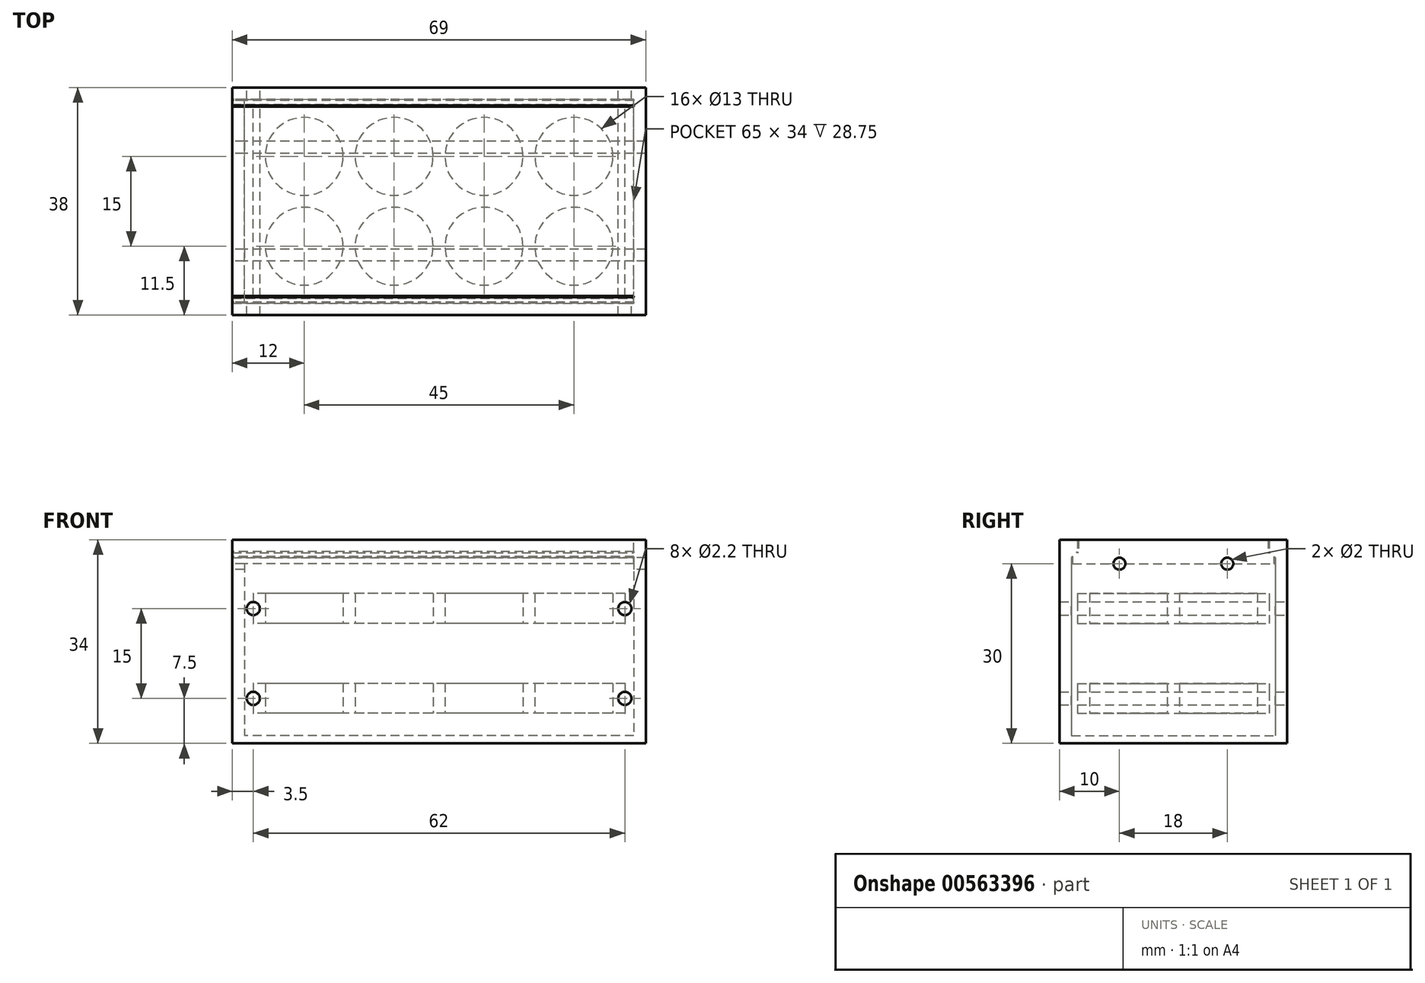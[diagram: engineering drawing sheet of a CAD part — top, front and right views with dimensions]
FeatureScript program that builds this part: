
annotation { "Feature Type Name" : "Feature", "Feature Type Description" : "" }
export const myFeature = defineFeature(function(context is Context, id is Id, definition is map)
    precondition{}
    {
        {
            var Q0;
            Q0=qCreatedBy(makeId("Top.planeOp"),FACE);
            var sketch = newSketch(context, id + "F0", { "sketchPlane" : qUnion([Q0])});
            skCircle(sketch, "E0", {"center": v(0, 0) * mm, "radius": 6.5 * mm});
            skCircle(sketch, "E1.0.1.0", {"center": v(0, 15) * mm, "radius": 6.5 * mm});
            skCircle(sketch, "E1.1.0.0", {"center": v(15, 0) * mm, "radius": 6.5 * mm});
            skCircle(sketch, "E1.1.1.0", {"center": v(15, 15) * mm, "radius": 6.5 * mm});
            skCircle(sketch, "E1.2.0.0", {"center": v(30, 0) * mm, "radius": 6.5 * mm});
            skCircle(sketch, "E1.2.1.0", {"center": v(30, 15) * mm, "radius": 6.5 * mm});
            skCircle(sketch, "E1.3.0.0", {"center": v(45, 0) * mm, "radius": 6.5 * mm});
            skCircle(sketch, "E1.3.1.0", {"center": v(45, 15) * mm, "radius": 6.5 * mm});
            skLineSegment(sketch, "E1.direction1", {"start": v(0, 0) * mm, "end": v(15, 0) * mm, "construction": true});
            skLineSegment(sketch, "E1.direction2", {"start": v(0, 0) * mm, "end": v(0, 15) * mm, "construction": true});
            skLineSegment(sketch, "E2.bottom", {"start": v(53.5, -8.5) * mm, "end": v(-8.5, -8.5) * mm});
            skLineSegment(sketch, "E2.top", {"start": v(53.5, 23.5) * mm, "end": v(-8.5, 23.5) * mm});
            skLineSegment(sketch, "E2.left", {"start": v(53.5, -8.5) * mm, "end": v(53.5, 23.5) * mm});
            skLineSegment(sketch, "E2.right", {"start": v(-8.5, -8.5) * mm, "end": v(-8.5, 23.5) * mm});
            skPoint(sketch, "E2.middle", {"position": v(22.5, 7.5) * mm});
            skPoint(sketch, "E2.middle.positionSnap0", {"position": v(0, 7.5) * mm});
            skPoint(sketch, "E2.centerSnap0", {"position": v(0, 7.5) * mm});
            skLineSegment(sketch, "E3", {"start": v(45, 15) * mm, "end": v(45, 0) * mm, "construction": true});
            skLineSegment(sketch, "E4", {"start": v(45, 7.5) * mm, "end": v(0, 7.5) * mm, "construction": true});
            skLineSegment(sketch, "E5.bottom", {"start": v(57, -11.5) * mm, "end": v(-12, -11.5) * mm});
            skLineSegment(sketch, "E5.top", {"start": v(57, 26.5) * mm, "end": v(-12, 26.5) * mm});
            skLineSegment(sketch, "E5.left", {"start": v(57, -11.5) * mm, "end": v(57, 26.5) * mm});
            skLineSegment(sketch, "E5.right", {"start": v(-12, -11.5) * mm, "end": v(-12, 26.5) * mm});
            skLineSegment(sketch, "E6.bottom", {"start": v(55, -9.5) * mm, "end": v(-10, -9.5) * mm});
            skLineSegment(sketch, "E6.top", {"start": v(55, 24.5) * mm, "end": v(-10, 24.5) * mm});
            skLineSegment(sketch, "E6.left", {"start": v(55, -9.5) * mm, "end": v(55, 24.5) * mm});
            skLineSegment(sketch, "E6.right", {"start": v(-10, -9.5) * mm, "end": v(-10, 24.5) * mm});
            skSolve(sketch);
        }
        {
            var Q0;
            Q0=makeQuery(id+"F0.imprint","IMPRINT",FACE,{"disambiguationData":[TD([[makeQuery(id+"F0.imprint","IMPRINT",EDGE,{"derivedFrom":sQuery(id+"F0.wireOp",EDGE,"E5.bottom")}),-1.0]])]});
            extrude(context, id + "F1", {"entities" : qUnion([Q0]), "depth" : 30 * mm, "offsetDistance" : 25 * mm});
        }
        {
            var Q0;
            Q0=makeQuery(id+"F0.imprint","IMPRINT",FACE,{"disambiguationData":[TD([[makeQuery(id+"F0.imprint","IMPRINT",EDGE,{"derivedFrom":sQuery(id+"F0.wireOp",EDGE,"E2.bottom")}),1.0]])]});
            var Q1;
            Q1=makeQuery(id+"F0.imprint","IMPRINT",FACE,{"disambiguationData":[TD([[makeQuery(id+"F0.imprint","IMPRINT",EDGE,{"derivedFrom":sQuery(id+"F0.wireOp",EDGE,"E1.0.1.0")}),1.0]])]});
            var Q2;
            Q2=makeQuery(id+"F0.imprint","IMPRINT",FACE,{"disambiguationData":[TD([[makeQuery(id+"F0.imprint","IMPRINT",EDGE,{"derivedFrom":sQuery(id+"F0.wireOp",EDGE,"E1.1.1.0")}),1.0]])]});
            var Q3;
            Q3=makeQuery(id+"F0.imprint","IMPRINT",FACE,{"disambiguationData":[TD([[makeQuery(id+"F0.imprint","IMPRINT",EDGE,{"derivedFrom":sQuery(id+"F0.wireOp",EDGE,"E1.2.1.0")}),1.0]])]});
            var Q4;
            Q4=makeQuery(id+"F0.imprint","IMPRINT",FACE,{"disambiguationData":[TD([[makeQuery(id+"F0.imprint","IMPRINT",EDGE,{"derivedFrom":sQuery(id+"F0.wireOp",EDGE,"E1.3.1.0")}),1.0]])]});
            var Q5;
            Q5=makeQuery(id+"F0.imprint","IMPRINT",FACE,{"disambiguationData":[TD([[makeQuery(id+"F0.imprint","IMPRINT",EDGE,{"derivedFrom":sQuery(id+"F0.wireOp",EDGE,"E1.3.0.0")}),1.0]])]});
            var Q6;
            Q6=makeQuery(id+"F0.imprint","IMPRINT",FACE,{"disambiguationData":[TD([[makeQuery(id+"F0.imprint","IMPRINT",EDGE,{"derivedFrom":sQuery(id+"F0.wireOp",EDGE,"E1.1.0.0")}),1.0]])]});
            var Q7;
            Q7=makeQuery(id+"F0.imprint","IMPRINT",FACE,{"disambiguationData":[TD([[makeQuery(id+"F0.imprint","IMPRINT",EDGE,{"derivedFrom":sQuery(id+"F0.wireOp",EDGE,"E0")}),-1.0]])]});
            var Q8;
            Q8=makeQuery(id+"F0.imprint","IMPRINT",FACE,{"disambiguationData":[TD([[makeQuery(id+"F0.imprint","IMPRINT",EDGE,{"derivedFrom":sQuery(id+"F0.wireOp",EDGE,"E1.2.0.0")}),1.0]])]});
            var Q9;
            Q9=makeQuery(id+"F0.imprint","IMPRINT",FACE,{"disambiguationData":[TD([[makeQuery(id+"F0.imprint","IMPRINT",EDGE,{"derivedFrom":sQuery(id+"F0.wireOp",EDGE,"E0")}),1.0]])]});
            extrude(context, id + "F2", {"entities" : qUnion([Q0, Q1, Q2, Q3, Q4, Q5, Q6, Q7, Q8, Q9]), "operationType" : NewBodyOperationType.ADD, "depth" : 1.25 * mm, "offsetDistance" : 25 * mm});
        }
        {
            var Q0;
            Q0=makeQuery(id+"F0.imprint","IMPRINT",FACE,{"disambiguationData":[TD([[makeQuery(id+"F0.imprint","IMPRINT",EDGE,{"derivedFrom":sQuery(id+"F0.wireOp",EDGE,"E0")}),-1.0]])]});
            extrude(context, id + "F3", {"entities" : qUnion([Q0]), "depth" : 10 * mm, "offsetDistance" : 25 * mm, "hasSecondDirection" : true, "secondDirectionOppositeDirection" : false, "secondDirectionDepth" : 5 * mm});
        }
        {
            var Q0;
            Q0=makeQuery(id+"F3.opExtrude","SWEPT_BODY",BODY,{"disambiguationData":[OSD([sQuery(id+"F0.wireOp",EDGE,"E0"),sQuery(id+"F0.wireOp",EDGE,"E1.0.1.0"),sQuery(id+"F0.wireOp",EDGE,"E1.1.0.0"),sQuery(id+"F0.wireOp",EDGE,"E1.1.1.0"),sQuery(id+"F0.wireOp",EDGE,"E1.2.0.0"),sQuery(id+"F0.wireOp",EDGE,"E1.2.1.0"),sQuery(id+"F0.wireOp",EDGE,"E1.3.0.0"),sQuery(id+"F0.wireOp",EDGE,"E1.3.1.0"),sQuery(id+"F0.wireOp",EDGE,"E2.bottom"),sQuery(id+"F0.wireOp",EDGE,"E2.top"),sQuery(id+"F0.wireOp",EDGE,"E2.left"),sQuery(id+"F0.wireOp",EDGE,"E2.right")])]});
            transform(context, id + "F4", {"entities" : qUnion([Q0]), "transformType" : TransformType.TRANSLATION_3D, "dx" : 0 * mm, "dy" : 0 * mm, "dz" : 15 * mm, "makeCopy" : true});
        }
        {
            var Q0;
            Q0=makeQuery(id+"F1.opExtrude","SWEPT_FACE",FACE,{"disambiguationData":[OSD([sQuery(id+"F0.wireOp",EDGE,"E5.top")])]});
            var sketch = newSketch(context, id + "F5", { "sketchPlane" : qUnion([Q0])});
            skCircle(sketch, "E7", {"center": v(8.5, 22.5) * mm, "radius": 1.1 * mm});
            skCircle(sketch, "E8", {"center": v(8.5, 7.5) * mm, "radius": 1.1 * mm});
            skCircle(sketch, "E9", {"center": v(-53.5, 7.5) * mm, "radius": 1.1 * mm});
            skCircle(sketch, "E10", {"center": v(-53.5, 22.5) * mm, "radius": 1.1 * mm});
            skSolve(sketch);
        }
        {
            var Q0;
            Q0 = qSketchRegion(id + "F5", true);
            extrude(context, id + "F6", {"entities" : qUnion([Q0]), "operationType" : NewBodyOperationType.REMOVE, "endBound" : BoundingType.SYMMETRIC, "oppositeDirection" : true, "depth" : 100 * mm, "offsetDistance" : 25 * mm});
        }
        {
            var Q0;
            Q0=makeQuery(id+"F1.opExtrude","SWEPT_FACE",FACE,{"disambiguationData":[OSD([sQuery(id+"F0.wireOp",EDGE,"E5.right")])]});
            var sketch = newSketch(context, id + "F7", { "sketchPlane" : qUnion([Q0])});
            skLineSegment(sketch, "E11", {"start": v(-26.5, 30) * mm, "end": v(-26.5, 34) * mm});
            skLineSegment(sketch, "E12", {"start": v(-26.5, 34) * mm, "end": v(-23.5, 34) * mm});
            skLineSegment(sketch, "E13", {"start": v(-23.5, 34) * mm, "end": v(-23.5, 32) * mm});
            skLineSegment(sketch, "E14", {"start": v(-23.5, 32) * mm, "end": v(-24.5, 32) * mm});
            skLineSegment(sketch, "E15", {"start": v(-24.5, 32) * mm, "end": v(-24.5, 30) * mm});
            skLineSegment(sketch, "E16", {"start": v(-7.5, 30) * mm, "end": v(-7.5, 34.07) * mm, "construction": true});
            skPoint(sketch, "E16.endSnap0", {"position": v(-7.5, 30) * mm});
            skLineSegment(sketch, "E17.MirrorCS", {"start": v(8.5, 32) * mm, "end": v(9.5, 32) * mm});
            skLineSegment(sketch, "E18.MirrorCS", {"start": v(11.5, 34) * mm, "end": v(8.5, 34) * mm});
            skLineSegment(sketch, "E19.MirrorCS", {"start": v(11.5, 30) * mm, "end": v(11.5, 34) * mm});
            skLineSegment(sketch, "E20.MirrorCS", {"start": v(8.5, 34) * mm, "end": v(8.5, 32) * mm});
            skLineSegment(sketch, "E21.MirrorCS", {"start": v(9.5, 32) * mm, "end": v(9.5, 30) * mm});
            skLineSegment(sketch, "E22", {"start": v(8.5, 34) * mm, "end": v(-23.5, 34) * mm});
            skLineSegment(sketch, "E23", {"start": v(-23.3, 34) * mm, "end": v(-23.3, 31.8) * mm});
            skLineSegment(sketch, "E24", {"start": v(-23.3, 31.8) * mm, "end": v(-24.3, 31.8) * mm});
            skLineSegment(sketch, "E25", {"start": v(-24.3, 31.8) * mm, "end": v(-24.3, 30) * mm});
            skLineSegment(sketch, "E26.MirrorCS", {"start": v(8.3, 34) * mm, "end": v(8.3, 31.8) * mm});
            skLineSegment(sketch, "E27.MirrorCS", {"start": v(8.3, 31.8) * mm, "end": v(9.3, 31.8) * mm});
            skLineSegment(sketch, "E28.MirrorCS", {"start": v(9.3, 31.8) * mm, "end": v(9.3, 30) * mm});
            skSolve(sketch);
        }
        {
            var Q0;
            {var subQ0=sQuery(id+"F7.wireOp",EDGE,"E11");Q0=makeQuery(id+"F7.imprint","IMPRINT",FACE,{"disambiguationData":[TD([[makeQuery(id+"F7.imprint","IMPRINT",EDGE,{"derivedFrom":subQ0}),-1.0]])]});}
            var Q1;
            Q1=makeQuery(id+"F7.imprint","IMPRINT",FACE,{"disambiguationData":[TD([[makeQuery(id+"F7.imprint","IMPRINT",EDGE,{"derivedFrom":sQuery(id+"F7.wireOp",EDGE,"E17.MirrorCS")}),1.0]])]});
            var Q2;
            Q2=makeQuery(id+"F1.opExtrude","SWEPT_FACE",FACE,{"disambiguationData":[OSD([sQuery(id+"F0.wireOp",EDGE,"E5.left")])]});
            extrude(context, id + "F8", {"entities" : qUnion([Q0, Q1]), "operationType" : NewBodyOperationType.ADD, "endBound" : BoundingType.UP_TO_SURFACE, "oppositeDirection" : true, "depth" : 25 * mm, "endBoundEntityFace" : qUnion([Q2]), "offsetDistance" : 25 * mm});
        }
        {
            var Q0;
            Q0=makeQuery(id+"F8.opExtrude","SWEPT_EDGE",EDGE,{"disambiguationData":[OSD([sQuery(id+"F7.wireOp",EDGE,"E14"),sQuery(id+"F7.wireOp",EDGE,"E15")])]});
            var Q1;
            Q1=makeQuery(id+"F8.opExtrude","SWEPT_EDGE",EDGE,{"disambiguationData":[OSD([sQuery(id+"F7.wireOp",EDGE,"E17.MirrorCS"),sQuery(id+"F7.wireOp",EDGE,"E21.MirrorCS")])]});
            chamfer(context, id + "F9", {"entities" : qUnion([Q0, Q1]), "width" : 1 * mm, "tangentPropagation" : true});
        }
        {
            var Q0;
            {var subQ3=sQuery(id+"F7.wireOp",EDGE,"E23");Q0=makeQuery(id+"F7.imprint","IMPRINT",FACE,{"disambiguationData":[TD([[makeQuery(id+"F7.imprint","IMPRINT",EDGE,{"derivedFrom":subQ3}),1.0]])]});}
            var Q1;
            Q1=makeQuery(id+"F1.opExtrude","SWEPT_FACE",FACE,{"disambiguationData":[OSD([sQuery(id+"F0.wireOp",EDGE,"E6.left")])]});
            extrude(context, id + "F10", {"entities" : qUnion([Q0]), "endBound" : BoundingType.UP_TO_SURFACE, "oppositeDirection" : true, "depth" : 25 * mm, "endBoundEntityFace" : qUnion([Q1]), "offsetDistance" : 25 * mm});
        }
        {
            var Q0;
            {var subQ0=sQuery(id+"F0.wireOp",EDGE,"E6.left");var subQ1=sQuery(id+"F0.wireOp",EDGE,"E5.left");var subQ2=sQuery(id+"F0.wireOp",EDGE,"E6.top");var subQ3=sQuery(id+"F0.wireOp",EDGE,"E6.bottom");Q0=makeQuery(id+"F8.boolean.opBoolean","SPLIT",FACE,{"disambiguationData":[TD([makeQuery(id+"F1.opExtrude","SWEPT_FACE",FACE,{"disambiguationData":[OSD([subQ1])]})])],"derivedFrom":makeQuery(id+"F1.opExtrude","CAP_FACE",FACE,{"disambiguationData":[OSD([sQuery(id+"F0.wireOp",EDGE,"E5.bottom"),sQuery(id+"F0.wireOp",EDGE,"E5.top"),subQ1,sQuery(id+"F0.wireOp",EDGE,"E5.right"),subQ3,subQ2,subQ0,sQuery(id+"F0.wireOp",EDGE,"E6.right")])],"isStart":false})});}
            var Q1;
            Q1=makeQuery(id+"F8.opExtrude","SWEPT_FACE",FACE,{"disambiguationData":[OSD([sQuery(id+"F7.wireOp",EDGE,"E18.MirrorCS")])]});
            extrude(context, id + "F11", {"entities" : qUnion([Q0]), "operationType" : NewBodyOperationType.ADD, "endBound" : BoundingType.UP_TO_SURFACE, "depth" : 25 * mm, "endBoundEntityFace" : qUnion([Q1]), "offsetDistance" : 25 * mm});
        }
        {
            var Q0;
            {var subQ0=sQuery(id+"F0.wireOp",EDGE,"E5.right");Q0=makeQuery(id+"F7.imprint","IMPRINT",FACE,{"disambiguationData":[TD([[makeQuery(id+"F7.imprint","IMPRINT",EDGE,{"derivedFrom":makeQuery(id+"F1.opExtrude","CAP_EDGE",EDGE,{"disambiguationData":[OSD([subQ0])],"isStart":true})}),-1.0]])]});}
            var sketch = newSketch(context, id + "F12", { "sketchPlane" : qUnion([Q0])});
            skCircle(sketch, "E29", {"center": v(-16.5, 30) * mm, "radius": 1 * mm});
            skCircle(sketch, "E30", {"center": v(1.5, 30) * mm, "radius": 1 * mm});
            skSolve(sketch);
        }
        {
            var Q0;
            Q0 = qSketchRegion(id + "F12", true);
            var Q1;
            {var subQ0=sQuery(id+"F0.wireOp",EDGE,"E5.left");Q1=makeQuery(id+"F11.boolean.opBoolean","MERGE",FACE,{"derivedFrom":[makeQuery(id+"F8.boolean.opBoolean","MERGE",FACE,{"derivedFrom":[makeQuery(id+"F1.opExtrude","SWEPT_FACE",FACE,{"disambiguationData":[OSD([subQ0])]}),makeQuery(id+"F8.opExtrude","CAP_FACE",FACE,{"disambiguationData":[OSD([subQ0]),OD(0.0)],"isStart":false}),makeQuery(id+"F8.opExtrude","CAP_FACE",FACE,{"disambiguationData":[OSD([subQ0]),OD(1.0)],"isStart":false})]}),makeQuery(id+"F11.opExtrude","SWEPT_FACE",FACE,{"disambiguationData":[OSD([subQ0])]})]});}
            extrude(context, id + "F13", {"entities" : qUnion([Q0]), "operationType" : NewBodyOperationType.REMOVE, "endBound" : BoundingType.UP_TO_SURFACE, "oppositeDirection" : true, "depth" : 25 * mm, "endBoundEntityFace" : qUnion([Q1]), "offsetDistance" : 25 * mm});
        }
    });
